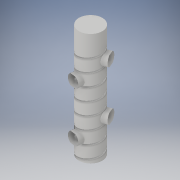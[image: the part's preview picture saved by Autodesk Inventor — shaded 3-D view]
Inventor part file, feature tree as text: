
AUTODESK INVENTOR PART (.ipt)
format: ipt  version: 2017 (Build 210142000, 142)  size: 926,720 bytes
history: native  units: in
note: dims shown in document units (in); Inventor stores cm internally (conversion verified against a paired STEP export)
features: extrude x25, other x15, sketch x14, loft x6, shell x1, plane x1, delete_face x1
ambient origin geometry x8: Origin, YZ Plane, XZ Plane, XY Plane, X Axis, Y Axis, Z Axis, Center Point
bodies: Body1 (feature_tree), Body2 (feature_tree)
feature tree (63):
  shell  "shell and ramp"  Thickness=15.0in
  extrude  "outer cassing"  Depth=72.0in TaperAngle=0.0deg
  extrude  "bottom"  Depth=3.5in
  other  "Work Axis1"
  other  "ramp"
  other  "top floor fill workplane"
  extrude  "top floor fill"  Depth=0.5in
  sketch  "Sketch5"  dims[d53=3.0in d54=0.5in]
  other  "railing complete"
  other  "light ramp to complete"
  extrude  "top cap"  Depth=9.0in
  plane  "workplane sketch"
  other  "connection plane 1"
  other  "connection plane 2"
  other  "connection workplane 3"
  extrude  "bottom connection"  TaperAngle=90.0deg  [1 undecoded]
  extrude  "bottom connect to case"  TaperAngle=90.0deg  [1 undecoded]
  extrude  "connection cut"  Depth=1.0in TaperAngle=0.0deg
  sketch  "Sketch20"  dims[d55=3.0in]
  extrude  "connetion 2"  Depth=9.48in
  extrude  "connection to case 2"  Depth=1.0in TaperAngle=0.0deg
  extrude  "connection cut 2"  Depth=6.6667in TaperAngle=0.0deg
  loft  "connection ramp 2"
  extrude  "connection 3"  Depth=30.81in
  extrude  "connection to case 3"  Depth=1.0in TaperAngle=0.0deg
  extrude  "connection cut 3"  Depth=1.0in TaperAngle=0.0deg
  loft  "connetion ramp 3"
  sketch  "Sketch23"  dims[d64=8.0in d65=1.0in d66=3.1201in d67=0.0in d68=90.0deg d69=90.0deg d70=0.0in d71=0.0in d146=9.0in]
  extrude  "connection 4"  Depth=6.6667in TaperAngle=0.0deg
  extrude  "connection to case 4"  Depth=1.0in TaperAngle=0.0deg
  extrude  "connection cut 4"  Depth=1.0in TaperAngle=0.0deg
  loft  "connection ramp 4"
  sketch  "Sketch24"  dims[d147=1.1811in d149=360.0deg d151=90.0deg]
  extrude  "connection 5"  Depth=6.6667in TaperAngle=0.0deg
  extrude  "connection to case 5"  Depth=1.0in TaperAngle=0.0deg
  extrude  "connection cut 5"  Depth=1.0in TaperAngle=0.0deg
  loft  "connection ramp 5"
  sketch  "Sketch25"  dims[d152=90.0deg d153=90.0deg]
  extrude  "connection 6"  Depth=62.8in
  extrude  "connection to case 6"  Depth=1.0in TaperAngle=0.0deg
  extrude  "connection cut 6"  Depth=1.0in TaperAngle=0.0deg
  loft  "connection ramp 6"
  sketch  "Sketch26"  dims[d154=6.6667in d157=4.8944in d158=1.0in d159=0.0in d160=1.0in d161=0.0in]
  extrude  "connection 7"  Depth=1.0in TaperAngle=0.0deg
  extrude  "connection to case 7"  Depth=1.0in TaperAngle=0.0deg
  extrude  "connection cut 7"  Depth=1.0in TaperAngle=0.0deg
  loft  "connection ramp 7"
  delete_face  "Delete Face1"
  sketch  "Sketch1"  dims[d1=16.0in d2=72.0in d3=0.0in]
  sketch  "Sketch4"  dims[d40=1.0in d41=0.0in d44=3.5in]
  sketch  "Sketch27"  dims[d162=2.6875in d163=0.0in d164=9.48in]
  sketch  "Sketch28"  dims[d165=6.6667in d168=4.8944in d169=1.0in d170=0.0in d171=1.0in d172=0.0in]
  other  "light railing complete"
  sketch  "Sketch29"  dims[d173=2.625in d174=0.0in d178=6.6667in d181=4.8944in d182=1.0in d183=0.0in]
  sketch  "Sketch30"  dims[d184=1.0in d185=0.0in d186=1.0in d187=0.0in]
  other  "Edges2"
  sketch  "Sketch32"  dims[d188=20.15in d189=30.81in]
  other  "Edges4"
  sketch  "Sketch33"  dims[d190=6.6667in d193=4.8944in d194=1.0in d195=0.0in d196=1.0in d197=0.0in d198=1.0in d199=0.0in d200=41.48in d201=6.6667in d204=4.8944in d205=1.0in d206=0.0in d207=1.0in d208=0.0in d209=1.0in d210=0.0in d211=52.15in d213=6.6667in d216=4.8944in d217=1.0in d218=0.0in d219=1.0in d220=0.0in d221=1.0in d222=0.0in d228=6.6667in d231=4.8944in d232=62.8in d233=1.0in d234=0.0in d237=1.0in d238=0.0in d239=0.0in d240=1.0in d241=0.0in d242=1.0in d243=0.0in d244=1.0in d245=0.0in d308=3.0in d309=0.5in d310=3.0in d321=90.0deg d322=90.0deg d323=0.0in d324=90.0deg d325=0.0in d326=90.0deg d327=1.0in d329=1.0in d330=0.0in d331=90.0deg d332=0.0in d333=90.0deg d335=1.0in d336=0.0in d337=90.0deg d338=0.0in d339=90.0deg d340=1.0in d341=0.0in d342=90.0deg d343=0.0in d344=90.0deg d346=1.0in d347=0.0in d348=90.0deg d349=0.0in d350=90.0deg d353=1.0in d354=0.0in d355=90.0deg d356=0.0in d357=90.0deg d448=4.0in d450=3.8873in d451=3.8873in d455=1.6458in d460=3.3333in d462=1.0in d477=4.0in d479=3.8873in d480=3.8873in d484=1.6458in d489=3.3333in d491=1.0in d492=4.0in d494=3.8873in d495=3.8873in d499=1.6458in d504=3.3333in d506=1.0in d507=4.0in d509=3.8873in d510=3.8873in d514=1.6458in d519=3.3333in d521=1.0in d522=4.0in d524=3.8873in d525=3.8873in d529=1.6458in d534=3.3333in d536=1.0in d537=4.0in d539=3.8873in d540=3.8873in d544=1.6458in d549=3.3333in d551=1.0in d552=4.0in d554=3.8873in d555=3.8873in d559=1.6458in d564=3.3333in d566=1.0in]
  other  "Edges5"
  other  "Edges6"
  other  "Edges1"
  other  "Edges3"
note: 2 required parameter values undecoded (feature->parameter linkage not recoverable at this tier; creation-order binding heuristic only, values carry confidence <= 0.55)
